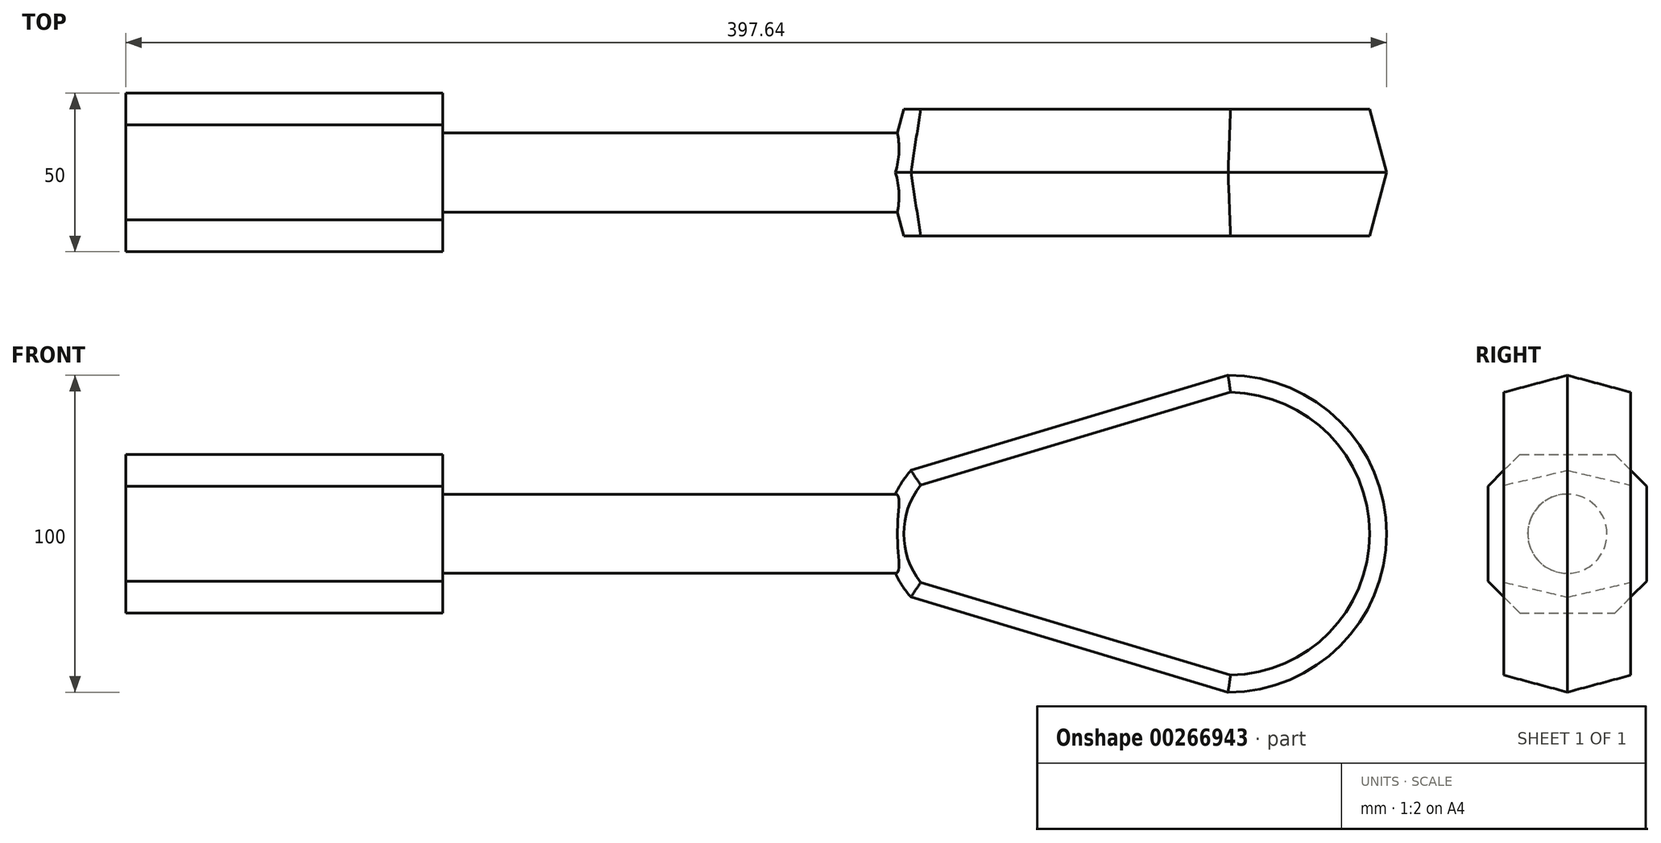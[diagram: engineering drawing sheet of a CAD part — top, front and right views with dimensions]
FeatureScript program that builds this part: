
annotation { "Feature Type Name" : "Feature", "Feature Type Description" : "" }
export const myFeature = defineFeature(function(context is Context, id is Id, definition is map)
    precondition{}
    {
        {
            var Q0;
            Q0=qCreatedBy(makeId("Right.planeOp"),FACE);
            var sketch = newSketch(context, id + "F0", { "sketchPlane" : qUnion([Q0])});
            skLineSegment(sketch, "E0.bottom", {"start": v(0, 0) * mm, "end": v(50, 0) * mm});
            skLineSegment(sketch, "E0.top", {"start": v(0, 50) * mm, "end": v(50, 50) * mm});
            skLineSegment(sketch, "E0.left", {"start": v(0, 0) * mm, "end": v(0, 50) * mm});
            skLineSegment(sketch, "E0.right", {"start": v(50, 0) * mm, "end": v(50, 50) * mm});
            skSolve(sketch);
        }
        {
            var Q0;
            Q0=makeQuery(id+"F0.imprint","IMPRINT",FACE,{"disambiguationData":[TD([[makeQuery(id+"F0.imprint","IMPRINT",EDGE,{"derivedFrom":sQuery(id+"F0.wireOp",EDGE,"E0.bottom")}),1.0]])]});
            extrude(context, id + "F1", {"entities" : qUnion([Q0]), "depth" : 100 * mm});
        }
        {
            var Q0;
            Q0=makeQuery(id+"F1.opExtrude","CAP_FACE",FACE,{"disambiguationData":[OSD([sQuery(id+"F0.wireOp",EDGE,"E0.bottom"),sQuery(id+"F0.wireOp",EDGE,"E0.top"),sQuery(id+"F0.wireOp",EDGE,"E0.left"),sQuery(id+"F0.wireOp",EDGE,"E0.right")])],"isStart":false});
            var sketch = newSketch(context, id + "F2", { "sketchPlane" : qUnion([Q0])});
            skCircle(sketch, "E1", {"center": v(25, 25) * mm, "radius": 12.5 * mm});
            skSolve(sketch);
        }
        {
            var Q0;
            Q0 = qSketchRegion(id + "F2", true);
            extrude(context, id + "F3", {"entities" : qUnion([Q0]), "operationType" : NewBodyOperationType.ADD, "depth" : 150 * mm});
        }
        {
            var Q0;
            Q0=qCreatedBy(makeId("Front.planeOp"),FACE);
            cPlane(context, id + "F4", {"entities" : qUnion([Q0]), "cplaneType" : CPlaneType.OFFSET, "offset" : 25 * mm, "oppositeDirection" : true, "width" : 150 * mm, "height" : 150 * mm});
        }
        {
            var Q0;
            Q0=qCreatedBy(id+"F4.planeOp",FACE);
            var sketch = newSketch(context, id + "F5", { "sketchPlane" : qUnion([Q0])});
            skArc(sketch, "E2", {"start": v(247.64, 45) * mm, "mid": v(240, 25) * mm, "end": v(247.64, 5) * mm});
            skLineSegment(sketch, "E3", {"start": v(247.64, 45) * mm, "end": v(347.64, 75) * mm});
            skLineSegment(sketch, "E4", {"start": v(226.54, 25) * mm, "end": v(374.9, 25) * mm, "construction": true});
            skPoint(sketch, "E4.startSnap0", {"position": v(240, 25) * mm});
            skPoint(sketch, "E4.endSnap0", {"position": v(240, 25) * mm});
            skLineSegment(sketch, "E5.MirrorCS", {"start": v(247.64, 5) * mm, "end": v(347.64, -25) * mm});
            skArc(sketch, "E6", {"start": v(347.64, -25) * mm, "mid": v(397.64, 25) * mm, "end": v(347.64, 75) * mm});
            skSolve(sketch);
        }
        {
            var Q0;
            Q0 = qSketchRegion(id + "F5", true);
            extrude(context, id + "F6", {"entities" : qUnion([Q0]), "operationType" : NewBodyOperationType.ADD, "endBound" : BoundingType.SYMMETRIC, "depth" : 40 * mm, "hasDraft" : true, "draftAngle" : 15 * degree, "draftPullDirection" : true});
        }
        {
            var Q0;
            Q0=makeQuery(id+"F1.opExtrude","SWEPT_EDGE",EDGE,{"disambiguationData":[OSD([sQuery(id+"F0.wireOp",EDGE,"E0.bottom"),sQuery(id+"F0.wireOp",EDGE,"E0.left")])]});
            var Q1;
            Q1=makeQuery(id+"F1.opExtrude","SWEPT_EDGE",EDGE,{"disambiguationData":[OSD([sQuery(id+"F0.wireOp",EDGE,"E0.bottom"),sQuery(id+"F0.wireOp",EDGE,"E0.right")])]});
            var Q2;
            Q2=makeQuery(id+"F1.opExtrude","SWEPT_EDGE",EDGE,{"disambiguationData":[OSD([sQuery(id+"F0.wireOp",EDGE,"E0.top"),sQuery(id+"F0.wireOp",EDGE,"E0.right")])]});
            var Q3;
            Q3=makeQuery(id+"F1.opExtrude","SWEPT_EDGE",EDGE,{"disambiguationData":[OSD([sQuery(id+"F0.wireOp",EDGE,"E0.top"),sQuery(id+"F0.wireOp",EDGE,"E0.left")])]});
            chamfer(context, id + "F7", {"entities" : qUnion([Q0, Q1, Q2, Q3]), "width" : 10 * mm, "tangentPropagation" : true});
        }
    });
